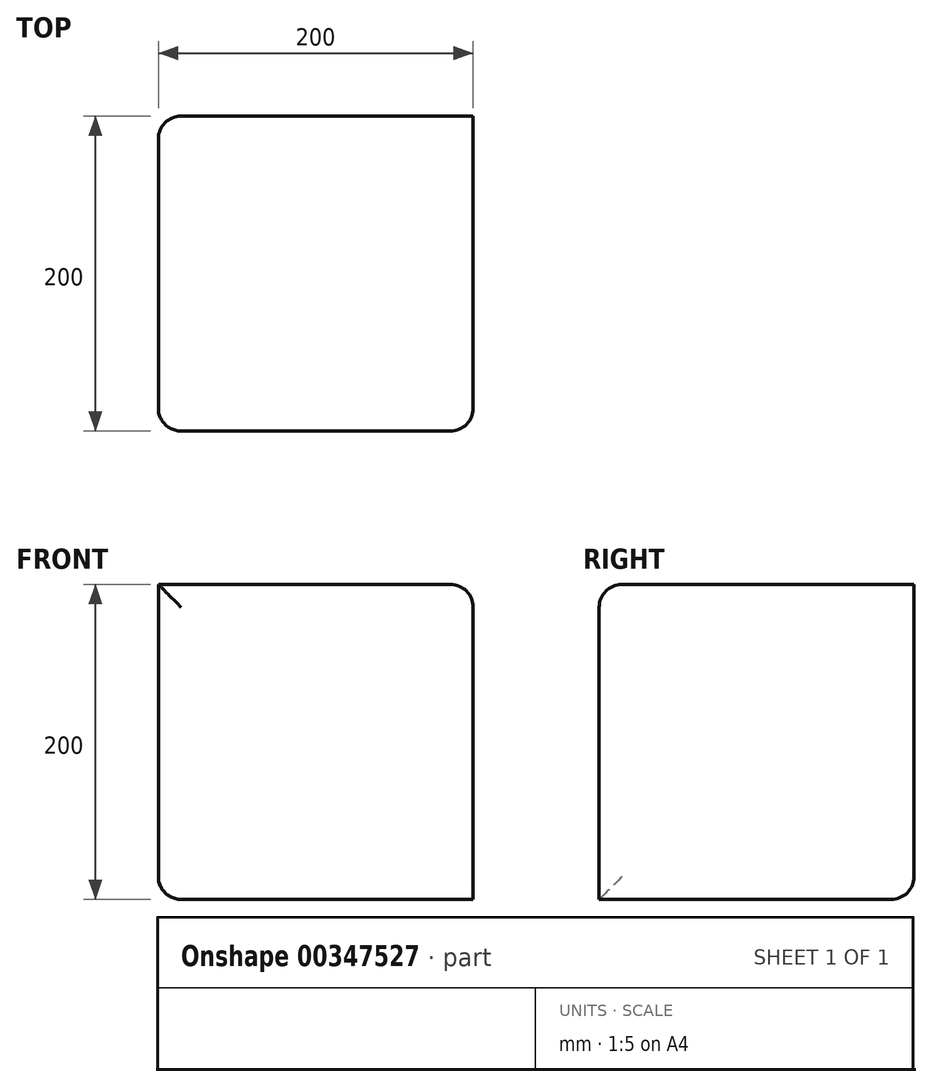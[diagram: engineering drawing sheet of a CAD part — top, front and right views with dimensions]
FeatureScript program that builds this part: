
annotation { "Feature Type Name" : "Feature", "Feature Type Description" : "" }
export const myFeature = defineFeature(function(context is Context, id is Id, definition is map)
    precondition{}
    {
        {
            var Q0;
            Q0=qCreatedBy(makeId("Front.planeOp"),FACE);
            var sketch = newSketch(context, id + "F0", { "sketchPlane" : qUnion([Q0])});
            skLineSegment(sketch, "E0.bottom", {"start": v(-100, 100) * mm, "end": v(100, 100) * mm});
            skLineSegment(sketch, "E0.top", {"start": v(-100, -100) * mm, "end": v(100, -100) * mm});
            skLineSegment(sketch, "E0.left", {"start": v(-100, 100) * mm, "end": v(-100, -100) * mm});
            skLineSegment(sketch, "E0.right", {"start": v(100, 100) * mm, "end": v(100, -100) * mm});
            skPoint(sketch, "E0.middle", {"position": v(0, 0) * mm});
            skSolve(sketch);
        }
        {
            var Q0;
            Q0 = qSketchRegion(id + "F0", true);
            extrude(context, id + "F1", {"entities" : qUnion([Q0]), "endBound" : BoundingType.SYMMETRIC, "depth" : 200 * mm});
        }
        {
            var Q0;
            Q0=makeQuery(id+"F1.opExtrude","CAP_EDGE",EDGE,{"disambiguationData":[OSD([sQuery(id+"F0.wireOp",EDGE,"E0.left")])],"isStart":false});
            var Q1;
            Q1=makeQuery(id+"F1.opExtrude","SWEPT_EDGE",EDGE,{"disambiguationData":[OSD([sQuery(id+"F0.wireOp",EDGE,"E0.bottom"),sQuery(id+"F0.wireOp",EDGE,"E0.right")])]});
            var Q2;
            Q2=makeQuery(id+"F1.opExtrude","SWEPT_EDGE",EDGE,{"disambiguationData":[OSD([sQuery(id+"F0.wireOp",EDGE,"E0.top"),sQuery(id+"F0.wireOp",EDGE,"E0.left")])]});
            var Q3;
            Q3=makeQuery(id+"F1.opExtrude","CAP_EDGE",EDGE,{"disambiguationData":[OSD([sQuery(id+"F0.wireOp",EDGE,"E0.bottom")])],"isStart":false});
            var Q4;
            Q4=makeQuery(id+"F1.opExtrude","CAP_EDGE",EDGE,{"disambiguationData":[OSD([sQuery(id+"F0.wireOp",EDGE,"E0.top")])],"isStart":true});
            var Q5;
            Q5=makeQuery(id+"F1.opExtrude","CAP_EDGE",EDGE,{"disambiguationData":[OSD([sQuery(id+"F0.wireOp",EDGE,"E0.right")])],"isStart":false});
            var Q6;
            Q6=makeQuery(id+"F1.opExtrude","CAP_EDGE",EDGE,{"disambiguationData":[OSD([sQuery(id+"F0.wireOp",EDGE,"E0.left")])],"isStart":true});
            fillet(context, id + "F2", {"entities" : qUnion([Q0, Q1, Q2, Q3, Q4, Q5, Q6]), "radius" : 14.5 * mm, "tangentPropagation" : true, "allowEdgeOverflow" : false});
        }
    });
